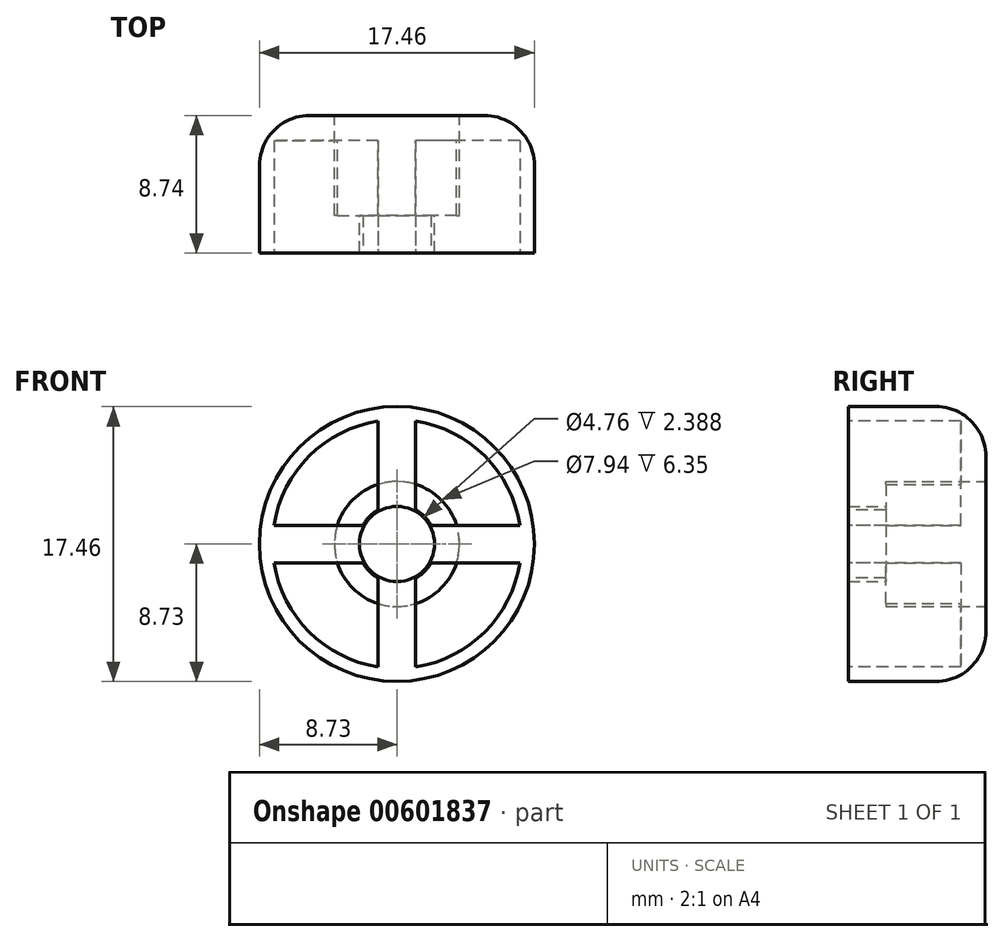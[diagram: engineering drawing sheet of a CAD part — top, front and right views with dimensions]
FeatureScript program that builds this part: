
annotation { "Feature Type Name" : "Feature", "Feature Type Description" : "" }
export const myFeature = defineFeature(function(context is Context, id is Id, definition is map)
    precondition{}
    {
        {
            var Q0;
            Q0=qCreatedBy(makeId("Front.planeOp"),FACE);
            var sketch = newSketch(context, id + "F0", { "sketchPlane" : qUnion([Q0])});
            skCircle(sketch, "E0", {"center": v(0, 0) * mm, "radius": 8.73 * mm});
            skCircle(sketch, "E1", {"center": v(0, 0) * mm, "radius": 7.94 * mm});
            skCircle(sketch, "E2", {"center": v(0, 0) * mm, "radius": 2.38 * mm});
            skSolve(sketch);
        }
        {
            var Q0;
            Q0=makeQuery(id+"F0.imprint","IMPRINT",FACE,{"disambiguationData":[TD([[makeQuery(id+"F0.imprint","IMPRINT",EDGE,{"derivedFrom":sQuery(id+"F0.wireOp",EDGE,"E0")}),1.0]])]});
            var Q1;
            Q1=makeQuery(id+"F0.imprint","IMPRINT",FACE,{"disambiguationData":[TD([[makeQuery(id+"F0.imprint","IMPRINT",EDGE,{"derivedFrom":sQuery(id+"F0.wireOp",EDGE,"E1")}),1.0]])]});
            var Q2;
            Q2=makeQuery(id+"F0.imprint","IMPRINT",FACE,{"disambiguationData":[TD([[makeQuery(id+"F0.imprint","IMPRINT",EDGE,{"derivedFrom":sQuery(id+"F0.wireOp",EDGE,"E2")}),1.0]])]});
            extrude(context, id + "F1", {"entities" : qUnion([Q0, Q1, Q2]), "depth" : 8.74 * mm, "offsetDistance" : 25.4 * mm});
        }
        {
            var Q0;
            Q0=makeQuery(id+"F1.opExtrude","CAP_FACE",FACE,{"disambiguationData":[OSD([sQuery(id+"F0.wireOp",EDGE,"E0")])],"isStart":false});
            var sketch = newSketch(context, id + "F2", { "sketchPlane" : qUnion([Q0])});
            skArc(sketch, "E3", {"start": v(2.16, 1.2) * mm, "mid": v(1.75, 1.75) * mm, "end": v(1.2, 2.16) * mm});
            skArc(sketch, "E4", {"start": v(-1.2, 7.8) * mm, "mid": v(-5.58, 5.58) * mm, "end": v(-7.8, 1.2) * mm});
            skLineSegment(sketch, "E5", {"start": v(-7.8, 1.2) * mm, "end": v(-2.16, 1.2) * mm});
            skLineSegment(sketch, "E6.MirrorCS", {"start": v(-7.8, -1.2) * mm, "end": v(-2.16, -1.2) * mm});
            skLineSegment(sketch, "E7.1.0", {"start": v(-1.2, -7.8) * mm, "end": v(-1.2, -2.16) * mm});
            skLineSegment(sketch, "E7.1.1", {"start": v(1.2, -7.8) * mm, "end": v(1.2, -2.16) * mm});
            skLineSegment(sketch, "E7.2.0", {"start": v(7.8, -1.2) * mm, "end": v(2.16, -1.2) * mm});
            skLineSegment(sketch, "E7.2.1", {"start": v(7.8, 1.2) * mm, "end": v(2.16, 1.2) * mm});
            skLineSegment(sketch, "E7.3.0", {"start": v(1.2, 7.8) * mm, "end": v(1.2, 2.16) * mm});
            skLineSegment(sketch, "E7.3.1", {"start": v(-1.2, 7.8) * mm, "end": v(-1.2, 2.16) * mm});
            skArc(sketch, "E8.trimOffspring", {"start": v(7.8, 1.2) * mm, "mid": v(5.58, 5.58) * mm, "end": v(1.2, 7.8) * mm});
            skArc(sketch, "E9.trimOffspring", {"start": v(-1.2, 2.16) * mm, "mid": v(-1.75, 1.75) * mm, "end": v(-2.16, 1.2) * mm});
            skArc(sketch, "E10.trimOffspring", {"start": v(1.2, -2.16) * mm, "mid": v(1.75, -1.75) * mm, "end": v(2.16, -1.2) * mm});
            skArc(sketch, "E11.trimOffspring", {"start": v(1.2, -7.8) * mm, "mid": v(5.58, -5.58) * mm, "end": v(7.8, -1.2) * mm});
            skArc(sketch, "E12.trimOffspring", {"start": v(-2.16, -1.2) * mm, "mid": v(-1.75, -1.75) * mm, "end": v(-1.2, -2.16) * mm});
            skArc(sketch, "E13.trimOffspring", {"start": v(-7.8, -1.2) * mm, "mid": v(-5.58, -5.58) * mm, "end": v(-1.2, -7.8) * mm});
            skSolve(sketch);
        }
        {
            var Q0;
            Q0 = qSketchRegion(id + "F2", true);
            extrude(context, id + "F3", {"entities" : qUnion([Q0]), "operationType" : NewBodyOperationType.REMOVE, "oppositeDirection" : true, "depth" : 7.15 * mm, "offsetDistance" : 25.4 * mm});
        }
        {
            var Q0;
            Q0=sQuery(id+"F0.wireOp",VERTEX,"E0.center");
            var Q1;
            Q1=makeQuery(id+"F1.opExtrude","SWEPT_BODY",BODY,{"disambiguationData":[OSD([sQuery(id+"F0.wireOp",EDGE,"E0")])]});
            hole(context, id + "F4", {"style" : HoleStyle.C_BORE, "endStyle" : HoleEndStyle.THROUGH, "oppositeDirection" : true, "holeDiameter" : 4.76 * mm, "cBoreDiameter" : 7.94 * mm, "cBoreDepth" : 6.35 * mm, "majorDiameter" : 6.35 * mm, "isTappedThrough" : true, "tappedDepth" : 12.7 * mm, "tapClearance" : 3, "locations" : qUnion([Q0]), "scope" : qUnion([Q1])});
        }
        {
            var Q0;
            Q0=makeQuery(id+"F1.opExtrude","CAP_EDGE",EDGE,{"disambiguationData":[OSD([sQuery(id+"F0.wireOp",EDGE,"E0")])],"isStart":true});
            fillet(context, id + "F5", {"entities" : qUnion([Q0]), "radius" : 3.17 * mm, "tangentPropagation" : true, "allowEdgeOverflow" : false});
        }
    });
